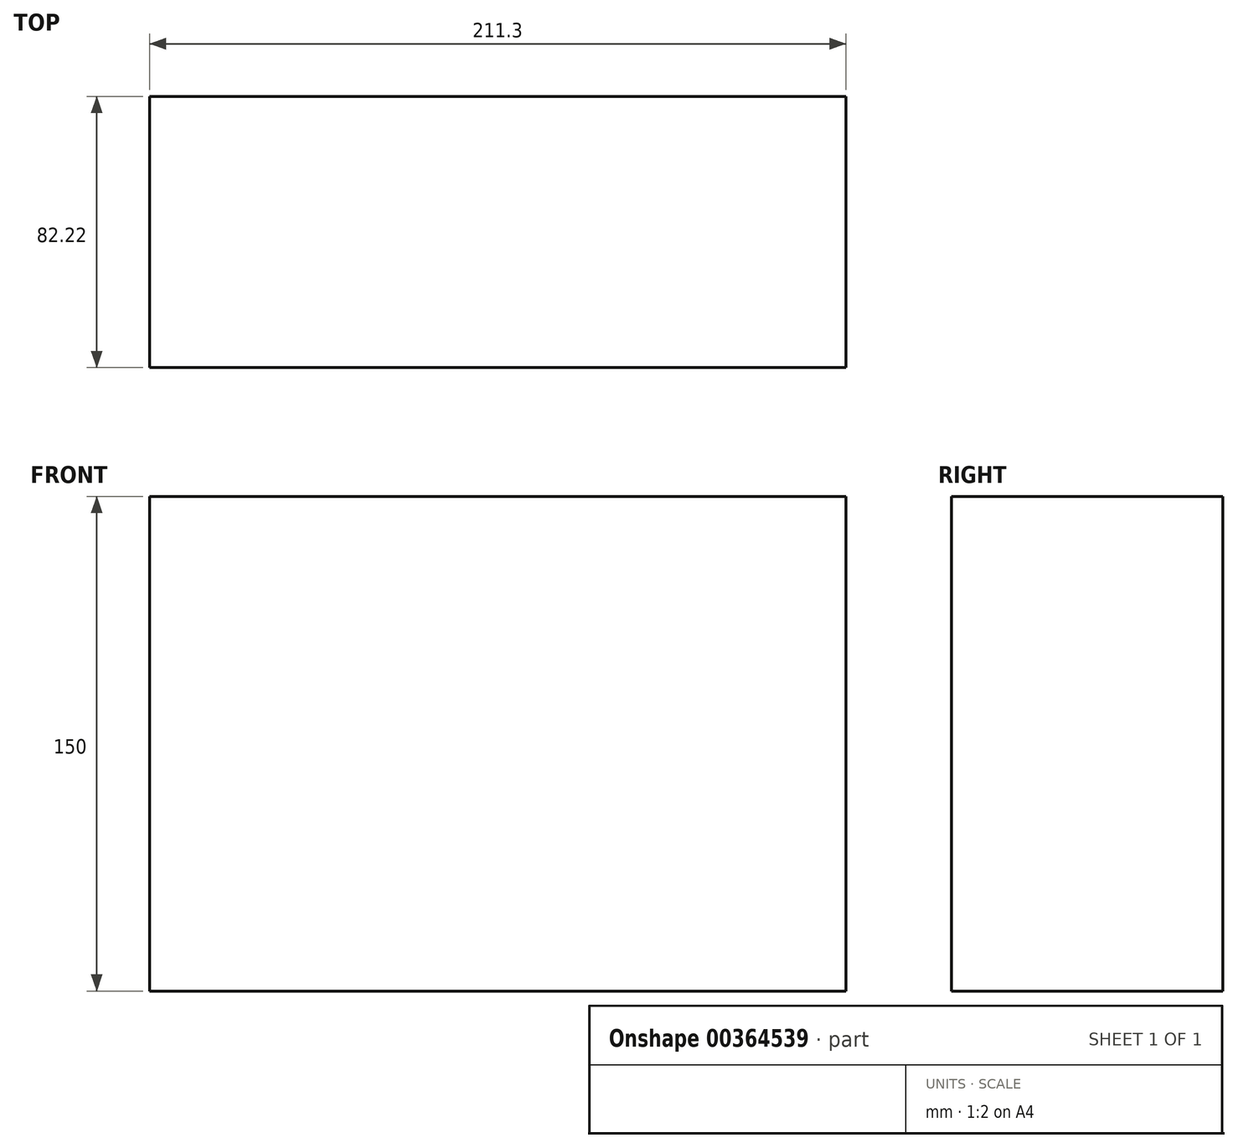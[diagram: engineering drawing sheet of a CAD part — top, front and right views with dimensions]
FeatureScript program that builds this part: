
annotation { "Feature Type Name" : "Feature", "Feature Type Description" : "" }
export const myFeature = defineFeature(function(context is Context, id is Id, definition is map)
    precondition{}
    {
        {
            var Q0;
            Q0=qCreatedBy(makeId("Top.planeOp"),FACE);
            var sketch = newSketch(context, id + "F0", { "sketchPlane" : qUnion([Q0])});
            skLineSegment(sketch, "E0.bottom", {"start": v(-126.06, 36.17) * mm, "end": v(85.24, 36.17) * mm});
            skLineSegment(sketch, "E0.top", {"start": v(-126.06, -46.05) * mm, "end": v(85.24, -46.05) * mm});
            skLineSegment(sketch, "E0.left", {"start": v(-126.06, 36.17) * mm, "end": v(-126.06, -46.05) * mm});
            skLineSegment(sketch, "E0.right", {"start": v(85.24, 36.17) * mm, "end": v(85.24, -46.05) * mm});
            skSolve(sketch);
        }
        {
            var Q0;
            Q0=makeQuery(id+"F0.imprint","IMPRINT",FACE,{"disambiguationData":[TD([[makeQuery(id+"F0.imprint","IMPRINT",EDGE,{"derivedFrom":sQuery(id+"F0.wireOp",EDGE,"E0.bottom")}),-1.0]])]});
            extrude(context, id + "F1", {"entities" : qUnion([Q0]), "depth" : 150 * mm});
        }
    });
